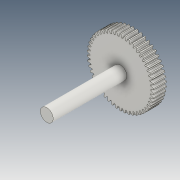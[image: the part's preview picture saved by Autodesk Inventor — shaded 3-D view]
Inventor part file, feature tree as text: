
AUTODESK INVENTOR PART (.ipt)
format: ipt  version: 2021 (Build 250183000, 183)  size: 334,336 bytes
history: native  units: mm (DEFAULTED — no unit token found)
features: plane x3, other x3, sketch x3, extrude x2
ambient origin geometry x8: Origin, YZ Plane, XZ Plane, XY Plane, X Axis, Y Axis, Z Axis, Center Point
bodies: Solid1 (feature_tree)
feature tree (11):
  extrude  "Extrusion1"  Depth=2.0mm TaperAngle=0.0deg
  plane  "Work Plane2"
  plane  "Work Plane8"
  plane  "Work Plane9"
  other  "Engrenagem reta"
  extrude  "Extrusão2"  Depth=10.0mm TaperAngle=0.0deg
  sketch  "Sketch1"  dims[d0=10.4mm d1=2.0mm d2=0.0mm]
  sketch  "Sketch2"  dims[d3=10.0mm d4=10.0mm d5=0.0mm]
  other  "Srf1"
  sketch  "Esboço3"  dims[d16=10.7mm d17=0.0mm d34=0.628319mm d39=0.0mm d41=0.0mm d43=10.7mm d46=10.7mm d47=0.0mm d48=0.0mm d49=11.5mm d50=0.0mm d51=0.5mm d52=0.872665mm]
  other  "Diâmetro do flanco"
